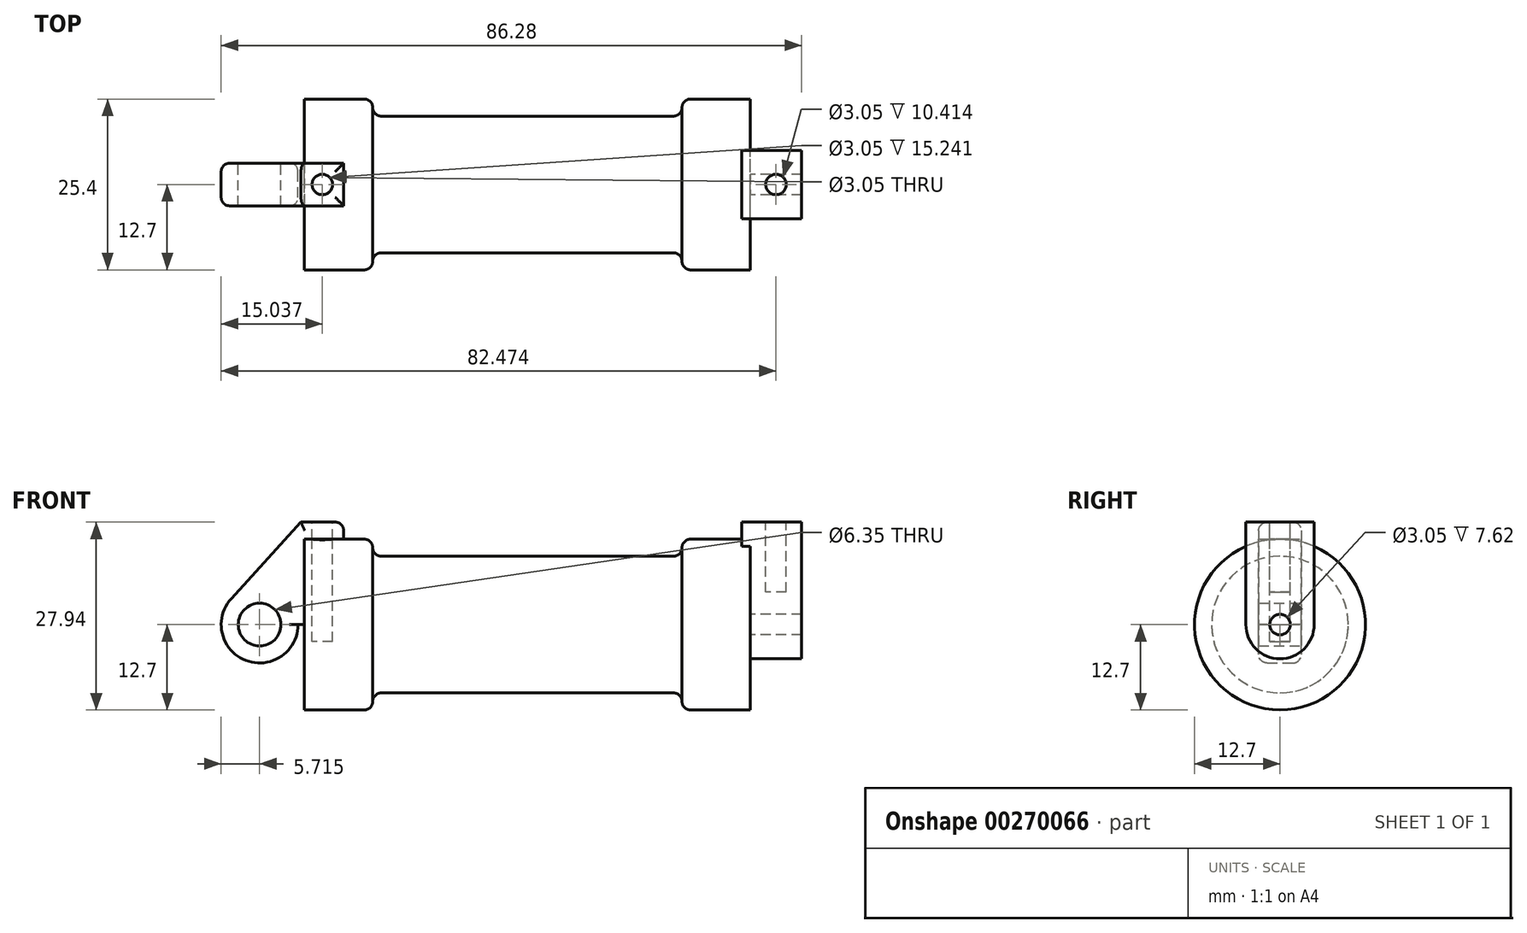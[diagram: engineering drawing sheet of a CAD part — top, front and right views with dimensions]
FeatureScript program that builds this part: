
annotation { "Feature Type Name" : "Feature", "Feature Type Description" : "" }
export const myFeature = defineFeature(function(context is Context, id is Id, definition is map)
    precondition{}
    {
        {
            var Q0;
            Q0=qCreatedBy(makeId("Front.planeOp"),FACE);
            var sketch = newSketch(context, id + "F0", { "sketchPlane" : qUnion([Q0])});
            skLineSegment(sketch, "E0", {"start": v(0, 0) * mm, "end": v(0, 12.7) * mm});
            skLineSegment(sketch, "E1", {"start": v(0, 12.7) * mm, "end": v(10.16, 12.7) * mm});
            skLineSegment(sketch, "E2", {"start": v(10.16, 12.7) * mm, "end": v(10.16, 10.16) * mm});
            skLineSegment(sketch, "E3", {"start": v(10.16, 10.16) * mm, "end": v(56.13, 10.16) * mm});
            skLineSegment(sketch, "E4", {"start": v(56.13, 10.16) * mm, "end": v(56.13, 12.7) * mm});
            skLineSegment(sketch, "E5", {"start": v(56.13, 12.7) * mm, "end": v(66.3, 12.7) * mm});
            skLineSegment(sketch, "E6", {"start": v(66.3, 12.7) * mm, "end": v(66.3, 0) * mm});
            skLineSegment(sketch, "E7", {"start": v(66.3, 0) * mm, "end": v(0, 0) * mm});
            skLineSegment(sketch, "E8", {"start": v(5.84, 15.24) * mm, "end": v(-0.5, 15.24) * mm});
            skLineSegment(sketch, "E9", {"start": v(-0.5, 15.24) * mm, "end": v(-10.88, 3.85) * mm});
            skLineSegment(sketch, "E10", {"start": v(0, 0) * mm, "end": v(-6.65, 0) * mm});
            skCircle(sketch, "E11", {"center": v(-6.65, 0) * mm, "radius": 5.72 * mm});
            skCircle(sketch, "E12", {"center": v(-6.65, 0) * mm, "radius": 3.18 * mm});
            skLineSegment(sketch, "E13", {"start": v(5.84, 15.24) * mm, "end": v(5.84, -9.4) * mm});
            skLineSegment(sketch, "E14", {"start": v(5.84, -9.4) * mm, "end": v(-8.18, -5.5) * mm});
            skSolve(sketch);
        }
        {
            var Q0;
            {var subQ4=sQuery(id+"F0.wireOp",EDGE,"E12");Q0=makeQuery(id+"F0.imprint","IMPRINT",FACE,{"disambiguationData":[TD([[makeQuery(id+"F0.imprint","IMPRINT",EDGE,{"derivedFrom":subQ4}),-1.0]])]});}
            var Q1;
            {var subQ3=sQuery(id+"F0.wireOp",EDGE,"E0");Q1=makeQuery(id+"F0.imprint","IMPRINT",FACE,{"disambiguationData":[TD([[makeQuery(id+"F0.imprint","IMPRINT",EDGE,{"derivedFrom":subQ3}),1.0]])]});}
            extrude(context, id + "F1", {"entities" : qUnion([Q0, Q1]), "endBound" : BoundingType.SYMMETRIC, "depth" : 6.35 * mm});
        }
        {
            var Q0;
            {var subQ0=sQuery(id+"F0.wireOp",EDGE,"E0");Q0=makeQuery(id+"F0.imprint","IMPRINT",FACE,{"disambiguationData":[TD([[makeQuery(id+"F0.imprint","IMPRINT",EDGE,{"derivedFrom":subQ0}),-1.0]])]});}
            var Q1;
            {var subQ0=sQuery(id+"F0.wireOp",EDGE,"E2");Q1=makeQuery(id+"F0.imprint","IMPRINT",FACE,{"disambiguationData":[TD([[makeQuery(id+"F0.imprint","IMPRINT",EDGE,{"derivedFrom":subQ0}),-1.0]])]});}
            var Q2;
            Q2=sQuery(id+"F0.wireOp",EDGE,"E7");
            revolve(context, id + "F2", {"entities" : qUnion([Q0, Q1]), "axis" : qUnion([Q2]), "revolveType" : RevolveType.FULL});
        }
        {
            var Q0;
            Q0=makeQuery(id+"F2.opRevolve","SWEPT_FACE",FACE,{"disambiguationData":[OSD([sQuery(id+"F0.wireOp",EDGE,"E6")])]});
            var sketch = newSketch(context, id + "F3", { "sketchPlane" : qUnion([Q0])});
            skLineSegment(sketch, "E15", {"start": v(0, 0) * mm, "end": v(12.7, 0) * mm, "construction": true});
            skLineSegment(sketch, "E16", {"start": v(12.7, 0) * mm, "end": v(-12.7, 0) * mm, "construction": true});
            skCircle(sketch, "E17", {"center": v(0, 0) * mm, "radius": 5.08 * mm});
            skCircle(sketch, "E18", {"center": v(0, 0) * mm, "radius": 1.52 * mm});
            skLineSegment(sketch, "E19", {"start": v(-5.08, 0) * mm, "end": v(-5.08, 15.24) * mm});
            skLineSegment(sketch, "E20", {"start": v(5.08, 0) * mm, "end": v(5.08, 15.24) * mm});
            skLineSegment(sketch, "E21", {"start": v(-5.08, 15.24) * mm, "end": v(5.08, 15.24) * mm});
            skSolve(sketch);
        }
        {
            var Q0;
            {var subQ0=sQuery(id+"F3.wireOp",EDGE,"E21");Q0=makeQuery(id+"F3.imprint","IMPRINT",FACE,{"disambiguationData":[TD([[makeQuery(id+"F3.imprint","IMPRINT",EDGE,{"derivedFrom":subQ0}),-1.0]])]});}
            var Q1;
            {var subQ0=sQuery(id+"F3.wireOp",EDGE,"E19");var subQ1=sQuery(id+"F3.wireOp",EDGE,"E17");var subQ2=makeQuery(id+"F3.imprint","INTERSECT",VERTEX,{"derivedFrom":[subQ1,subQ0]});Q1=makeQuery(id+"F3.imprint","IMPRINT",FACE,{"disambiguationData":[TD([[makeQuery(id+"F3.imprint","IMPRINT",EDGE,{"disambiguationData":[TD([[subQ2,1.0]])],"derivedFrom":subQ1}),-1.0]])]});}
            var Q2;
            Q2=makeQuery(id+"F3.imprint","IMPRINT",FACE,{"disambiguationData":[TD([[makeQuery(id+"F3.imprint","IMPRINT",EDGE,{"derivedFrom":sQuery(id+"F3.wireOp",EDGE,"E18")}),-1.0]])]});
            extrude(context, id + "F4", {"entities" : qUnion([Q0, Q1, Q2]), "operationType" : NewBodyOperationType.ADD, "depth" : 7.62 * mm});
        }
        {
            var Q0;
            Q0=makeQuery(id+"F4.opExtrude","SWEPT_FACE",FACE,{"disambiguationData":[OSD([sQuery(id+"F3.wireOp",EDGE,"E21")])]});
            var sketch = newSketch(context, id + "F5", { "sketchPlane" : qUnion([Q0])});
            skCircle(sketch, "E22", {"center": v(70.1, 0) * mm, "radius": 1.52 * mm});
            skSolve(sketch);
        }
        {
            var Q0;
            Q0=makeQuery(id+"F5.imprint","IMPRINT",FACE,{"disambiguationData":[TD([[makeQuery(id+"F5.imprint","IMPRINT",EDGE,{"derivedFrom":sQuery(id+"F5.wireOp",EDGE,"E22")}),1.0]])]});
            extrude(context, id + "F6", {"entities" : qUnion([Q0]), "operationType" : NewBodyOperationType.REMOVE, "oppositeDirection" : true, "depth" : 10.4 * mm});
        }
        {
            var Q0;
            Q0=makeQuery(id+"F4.opExtrude","CAP_FACE",FACE,{"disambiguationData":[OSD([sQuery(id+"F3.wireOp",EDGE,"E17"),sQuery(id+"F3.wireOp",EDGE,"E18"),sQuery(id+"F3.wireOp",EDGE,"E19"),sQuery(id+"F3.wireOp",EDGE,"E20"),sQuery(id+"F3.wireOp",EDGE,"E21")])],"isStart":true});
            extrude(context, id + "F7", {"entities" : qUnion([Q0]), "operationType" : NewBodyOperationType.ADD, "depth" : 1.27 * mm});
        }
        {
            var Q0;
            Q0=makeQuery(id+"F1.opExtrude","SWEPT_FACE",FACE,{"disambiguationData":[OSD([sQuery(id+"F0.wireOp",EDGE,"E8")])]});
            var sketch = newSketch(context, id + "F8", { "sketchPlane" : qUnion([Q0])});
            skCircle(sketch, "E23", {"center": v(2.67, 0) * mm, "radius": 1.52 * mm});
            skSolve(sketch);
        }
        {
            var Q0;
            Q0=makeQuery(id+"F8.imprint","IMPRINT",FACE,{"disambiguationData":[TD([[makeQuery(id+"F8.imprint","IMPRINT",EDGE,{"derivedFrom":sQuery(id+"F8.wireOp",EDGE,"E23")}),1.0]])]});
            extrude(context, id + "F9", {"entities" : qUnion([Q0]), "operationType" : NewBodyOperationType.REMOVE, "oppositeDirection" : true, "depth" : 17.78 * mm});
        }
        {
            var Q0;
            Q0=makeQuery(id+"F2.opRevolve","SWEPT_EDGE",EDGE,{"disambiguationData":[OSD([sQuery(id+"F0.wireOp",EDGE,"E4"),sQuery(id+"F0.wireOp",EDGE,"E5")])]});
            var Q1;
            Q1=makeQuery(id+"F2.opRevolve","SWEPT_EDGE",EDGE,{"disambiguationData":[OSD([sQuery(id+"F0.wireOp",EDGE,"E3"),sQuery(id+"F0.wireOp",EDGE,"E4")])]});
            var Q2;
            Q2=makeQuery(id+"F2.opRevolve","SWEPT_EDGE",EDGE,{"disambiguationData":[OSD([sQuery(id+"F0.wireOp",EDGE,"E1"),sQuery(id+"F0.wireOp",EDGE,"E2")])]});
            var Q3;
            Q3=makeQuery(id+"F2.opRevolve","SWEPT_EDGE",EDGE,{"disambiguationData":[OSD([sQuery(id+"F0.wireOp",EDGE,"E2"),sQuery(id+"F0.wireOp",EDGE,"E3")])]});
            fillet(context, id + "F10", {"entities" : qUnion([Q0, Q1, Q2, Q3]), "radius" : 1.27 * mm, "tangentPropagation" : true, "allowEdgeOverflow" : false});
        }
        {
            var Q0;
            Q0=makeQuery(id+"F1.opExtrude","SWEPT_EDGE",EDGE,{"disambiguationData":[OSD([sQuery(id+"F0.wireOp",EDGE,"E8"),sQuery(id+"F0.wireOp",EDGE,"E13")])]});
            var Q1;
            Q1=makeQuery(id+"F1.opExtrude","CAP_EDGE",EDGE,{"disambiguationData":[OSD([sQuery(id+"F0.wireOp",EDGE,"E8")])],"isStart":true});
            var Q2;
            Q2=makeQuery(id+"F1.opExtrude","CAP_EDGE",EDGE,{"disambiguationData":[OSD([sQuery(id+"F0.wireOp",EDGE,"E8")])],"isStart":false});
            var Q3;
            Q3=makeQuery(id+"F1.opExtrude","CAP_EDGE",EDGE,{"disambiguationData":[OSD([sQuery(id+"F0.wireOp",EDGE,"E9")])],"isStart":true});
            var Q4;
            Q4=makeQuery(id+"F1.opExtrude","CAP_EDGE",EDGE,{"disambiguationData":[OSD([sQuery(id+"F0.wireOp",EDGE,"E11")])],"isStart":true});
            var Q5;
            Q5=makeQuery(id+"F2.opRevolve","SWEPT_EDGE",EDGE,{"disambiguationData":[OSD([sQuery(id+"F0.wireOp",EDGE,"E0"),sQuery(id+"F0.wireOp",EDGE,"E1")])]});
            var Q6;
            Q6=makeQuery(id+"F1.opExtrude","CAP_EDGE",EDGE,{"disambiguationData":[OSD([sQuery(id+"F0.wireOp",EDGE,"E9")])],"isStart":false});
            var Q7;
            Q7=makeQuery(id+"F4.boolean.opBoolean","SPLIT",EDGE,{"disambiguationData":[OD(1.0)],"derivedFrom":makeQuery(id+"F2.opRevolve","SWEPT_EDGE",EDGE,{"disambiguationData":[OSD([sQuery(id+"F0.wireOp",EDGE,"E5"),sQuery(id+"F0.wireOp",EDGE,"E6")])]})});
            var Q8;
            Q8=makeQuery(id+"F4.opExtrude","CAP_EDGE",EDGE,{"disambiguationData":[OSD([sQuery(id+"F3.wireOp",EDGE,"E19")])],"isStart":false});
            var Q9;
            Q9=makeQuery(id+"F4.opExtrude","CAP_EDGE",EDGE,{"disambiguationData":[OSD([sQuery(id+"F3.wireOp",EDGE,"E17")])],"isStart":false});
            var Q10;
            Q10=makeQuery(id+"F4.opExtrude","CAP_EDGE",EDGE,{"disambiguationData":[OSD([sQuery(id+"F3.wireOp",EDGE,"E20")])],"isStart":false});
            var Q11;
            {var subQ0=sQuery(id+"F3.wireOp",EDGE,"E19");var subQ1=sQuery(id+"F3.wireOp",EDGE,"E17");Q11=makeQuery(id+"F4.boolean.opBoolean","SPLIT",EDGE,{"disambiguationData":[TD([makeQuery(id+"F4.opExtrude","SWEPT_FACE",FACE,{"disambiguationData":[OSD([subQ1])]})])],"derivedFrom":makeQuery(id+"F4.opExtrude","CAP_EDGE",EDGE,{"disambiguationData":[OSD([subQ0])],"isStart":true})});}
            var Q12;
            Q12=makeQuery(id+"F4.opExtrude","CAP_EDGE",EDGE,{"disambiguationData":[OSD([sQuery(id+"F3.wireOp",EDGE,"E17")])],"isStart":true});
            var Q13;
            {var subQ0=sQuery(id+"F3.wireOp",EDGE,"E20");var subQ1=sQuery(id+"F3.wireOp",EDGE,"E17");Q13=makeQuery(id+"F4.boolean.opBoolean","SPLIT",EDGE,{"disambiguationData":[TD([makeQuery(id+"F4.opExtrude","SWEPT_FACE",FACE,{"disambiguationData":[OSD([subQ1])]})])],"derivedFrom":makeQuery(id+"F4.opExtrude","CAP_EDGE",EDGE,{"disambiguationData":[OSD([subQ0])],"isStart":true})});}
            var Q14;
            Q14=makeQuery(id+"F7.opExtrude","CAP_EDGE",EDGE,{"disambiguationData":[OSD([sQuery(id+"F3.wireOp",EDGE,"E21")])],"isStart":false});
            var Q15;
            Q15=makeQuery(id+"F7.opExtrude","CAP_EDGE",EDGE,{"disambiguationData":[OSD([sQuery(id+"F0.wireOp",EDGE,"E5"),sQuery(id+"F0.wireOp",EDGE,"E6")])],"isStart":false});
            var Q16;
            {var subQ0=sQuery(id+"F3.wireOp",EDGE,"E21");var subQ1=sQuery(id+"F3.wireOp",EDGE,"E19");Q16=makeQuery(id+"F7.boolean.opBoolean","MERGE",EDGE,{"derivedFrom":[makeQuery(id+"F4.opExtrude","SWEPT_EDGE",EDGE,{"disambiguationData":[OSD([subQ1,subQ0])]}),makeQuery(id+"F7.opExtrude","SWEPT_EDGE",EDGE,{"disambiguationData":[OSD([subQ1,subQ0])]})]});}
            var Q17;
            {var subQ0=sQuery(id+"F3.wireOp",EDGE,"E19");var subQ1=sQuery(id+"F3.wireOp",EDGE,"E21");var subQ2=sQuery(id+"F3.wireOp",EDGE,"E20");var subQ3=sQuery(id+"F3.wireOp",EDGE,"E18");var subQ4=sQuery(id+"F3.wireOp",EDGE,"E17");var subQ5=sQuery(id+"F0.wireOp",EDGE,"E6");var subQ6=sQuery(id+"F0.wireOp",EDGE,"E5");Q17=makeQuery(id+"F7.opExtrude","SWEPT_EDGE",EDGE,{"disambiguationData":[OSD([subQ6,subQ5,subQ4,subQ3,subQ0,subQ2,subQ1]),TDD([makeQuery(id+"F4.boolean.opBoolean","TWEAK_VERTEX",VERTEX,{"derivedFrom":[makeQuery(id+"F2.opRevolve","SWEPT_FACE",FACE,{"disambiguationData":[OSD([subQ6])]}),makeQuery(id+"F2.opRevolve","SWEPT_FACE",FACE,{"disambiguationData":[OSD([subQ5])]}),makeQuery(id+"F4.opExtrude","CAP_FACE",FACE,{"disambiguationData":[OSD([subQ4,subQ3,subQ0,subQ2,subQ1])],"isStart":true}),makeQuery(id+"F4.opExtrude","SWEPT_FACE",FACE,{"disambiguationData":[OSD([subQ0])]})]})])]});}
            var Q18;
            Q18=makeQuery(id+"F7.opExtrude","CAP_EDGE",EDGE,{"disambiguationData":[OSD([sQuery(id+"F3.wireOp",EDGE,"E20")])],"isStart":false});
            var Q19;
            {var subQ0=sQuery(id+"F3.wireOp",EDGE,"E20");var subQ1=sQuery(id+"F3.wireOp",EDGE,"E21");var subQ2=sQuery(id+"F3.wireOp",EDGE,"E19");var subQ3=sQuery(id+"F3.wireOp",EDGE,"E18");var subQ4=sQuery(id+"F3.wireOp",EDGE,"E17");var subQ5=sQuery(id+"F0.wireOp",EDGE,"E6");var subQ6=sQuery(id+"F0.wireOp",EDGE,"E5");Q19=makeQuery(id+"F7.opExtrude","SWEPT_EDGE",EDGE,{"disambiguationData":[OSD([subQ6,subQ5,subQ4,subQ3,subQ2,subQ0,subQ1]),TDD([makeQuery(id+"F4.boolean.opBoolean","TWEAK_VERTEX",VERTEX,{"derivedFrom":[makeQuery(id+"F2.opRevolve","SWEPT_FACE",FACE,{"disambiguationData":[OSD([subQ6])]}),makeQuery(id+"F2.opRevolve","SWEPT_FACE",FACE,{"disambiguationData":[OSD([subQ5])]}),makeQuery(id+"F4.opExtrude","CAP_FACE",FACE,{"disambiguationData":[OSD([subQ4,subQ3,subQ2,subQ0,subQ1])],"isStart":true}),makeQuery(id+"F4.opExtrude","SWEPT_FACE",FACE,{"disambiguationData":[OSD([subQ0])]})]})])]});}
            var Q20;
            {var subQ0=sQuery(id+"F3.wireOp",EDGE,"E21");var subQ1=sQuery(id+"F3.wireOp",EDGE,"E20");Q20=makeQuery(id+"F7.boolean.opBoolean","MERGE",EDGE,{"derivedFrom":[makeQuery(id+"F4.opExtrude","SWEPT_EDGE",EDGE,{"disambiguationData":[OSD([subQ1,subQ0])]}),makeQuery(id+"F7.opExtrude","SWEPT_EDGE",EDGE,{"disambiguationData":[OSD([subQ1,subQ0])]})]});}
            var Q21;
            Q21=makeQuery(id+"F7.opExtrude","CAP_EDGE",EDGE,{"disambiguationData":[OSD([sQuery(id+"F3.wireOp",EDGE,"E19")])],"isStart":false});
            var Q22;
            Q22=makeQuery(id+"F4.opExtrude","CAP_EDGE",EDGE,{"disambiguationData":[OSD([sQuery(id+"F3.wireOp",EDGE,"E21")])],"isStart":false});
            fillet(context, id + "F11", {"entities" : qUnion([Q0, Q1, Q2, Q3, Q4, Q5, Q6, Q7, Q8, Q9, Q10, Q11, Q12, Q13, Q14, Q15, Q16, Q17, Q18, Q19, Q20, Q21, Q22]), "radius" : 1.27 * mm, "tangentPropagation" : true, "allowEdgeOverflow" : false});
        }
    });
